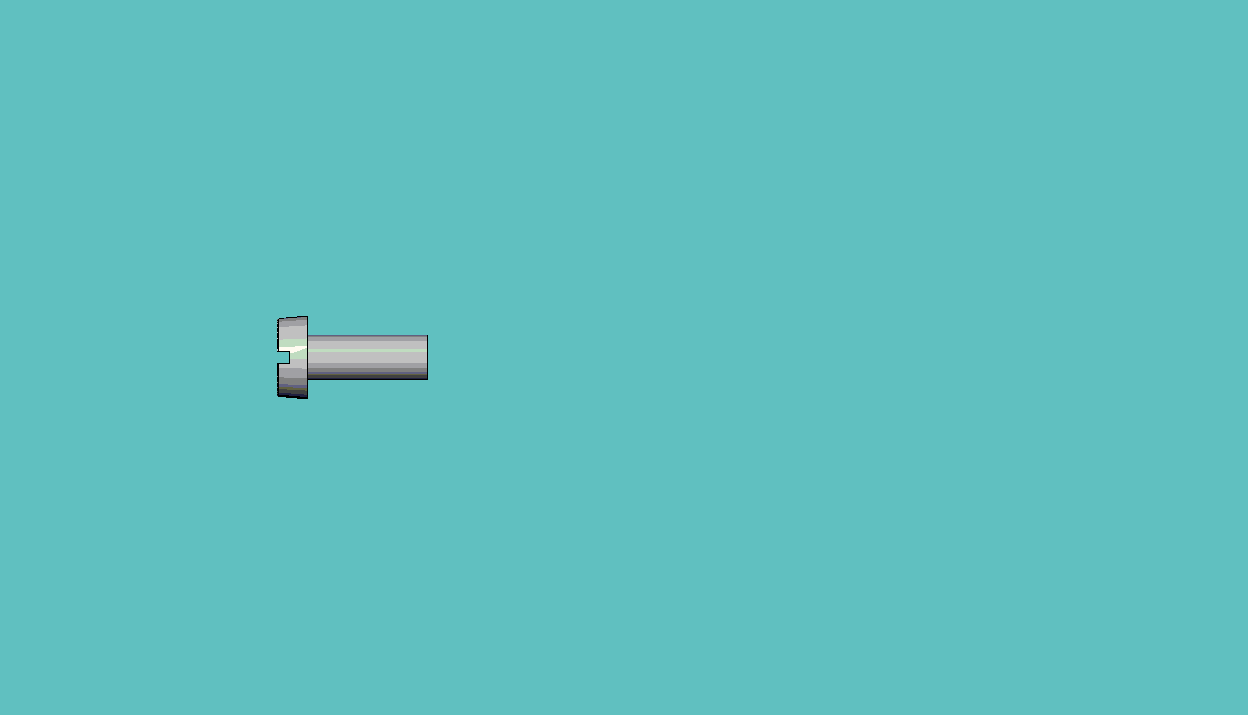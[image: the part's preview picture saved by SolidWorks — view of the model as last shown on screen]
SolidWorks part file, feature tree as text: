
SOLIDWORKS PART (.sldprt)
format: sldprt  version: not decoded by parser v0  size: 142,848 bytes
history: native  units: mm
features: plane x3, sketch x3, fillet x2, material x1, revolve x1, thread x1, cut_extrude x1, cut_revolve x1, pattern_linear x1 (+10 scaffold rows collapsed; 1 parser-record rows omitted)
feature tree (25):
  scaffold x10  (default folders/planes/origin — collapsed)
  material  "Material <not specified>"
  plane  "Plane1"
  plane  "Plane2"
  plane  "Plane3"
  parser-record x1  (decoder bookkeeping rows leaked as tree rows — omitted from the tree; the rows remain in map.json)
  revolve  "Base-Revolve"  [1 undecoded]
  sketch  "BodySke"  dims[c1.Head_fillet_rad=3.6322mm c1.D1=~7.099516mm c1.Head_ang=85.0deg c1.Oval_ht=2.3876mm c1.Head_ht=6.1976mm c1.Diameter=9.525mm c1.Length=76.2mm c1.Head_dia=20.0152mm c2.Head_dia=15.3924mm c2.Head_ht=8.509mm c2.Length=8.0mm c2.Head_side_ht=6.1722mm c3.Head_ht=2.0mm c3.Head_dia=18.4912mm c3.Advance=0.5mm c3.Thread_nom=8.0mm c3.Thread_lim=36.5125mm c4.Head_dia=5.5mm c4.D2=152.4mm c4.Head_side_angle=5.0deg c4.Diameter=3.0mm]
  thread  "ThreadCosmetic"  Diameter=7mm Thread_length=7mm Thread_minor=2.439mm  [1 undecoded]
  fillet  "Fillet1"  Radius=0.1mm Head_dia=5.5mm Diameter=3mm
  fillet  "Fillet2"  Radius=0.1mm
  sketch  "Sketch2"  dims[D1=5.5mm Slot_width=0.8mm D2=2.75mm D3=0.4mm]
  cut_extrude  "Slot"  Depth=0.85mm Slot_depth=0.85mm
  sketch  "ThdSchSke"  dims[c1.Thread_minor=~1.03886mm c1.Diameter=~1.413535mm c1.Start=~0.988134mm c1.D4=~4.446753mm c1.Vee=60.0deg c2.Thread_minor=~1.03886mm c2.Start=~2.540025mm c2.D1=~0.108159mm c2.D2=~0.108159mm c3.D1=~0.216319mm c3.SideAngle=55.0deg c3.D2=~0.216319mm c3.VeeAngle=70.0deg c3.Thread_minor=2.439mm c3.Overcut=3.75mm c3.Diameter=3.0mm c3.D6=~8.326268mm c4.D1=~8.326268mm c5.D1=90.0deg c5.Start=11.1125mm c6.Start=~44.450025mm c7.Start=3.0mm]
  cut_revolve  "ThreadSchematic"  Angle=360deg
  pattern_linear  "ThdSchPat"  Count1=15 Count2=1 Spacing1=0.5mm Spacing2=50mm Num_threads=15 Advance=0.5mm CopiedFlag=1
decode coverage: 9 of 10 modeling features carry decoded parameters
note: ~ marks probable driven/reference dimensions
note: 2 parameter values undecoded
note: suppression state not decoded; provenance and decode notes live in map.json
